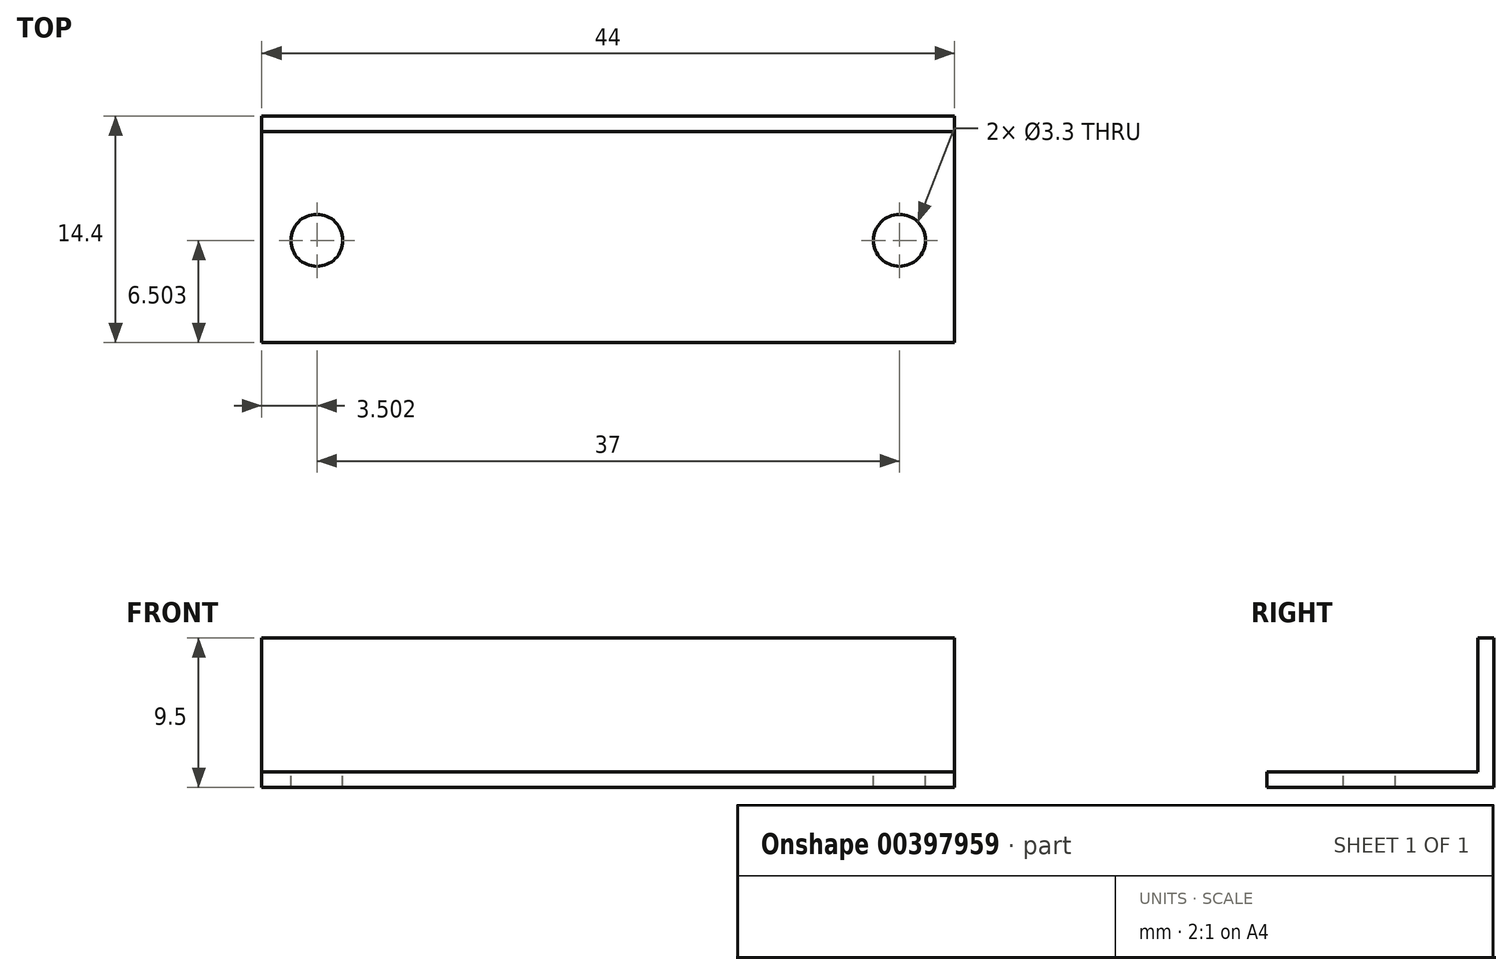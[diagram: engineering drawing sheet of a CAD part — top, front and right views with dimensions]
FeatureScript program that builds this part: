
annotation { "Feature Type Name" : "Feature", "Feature Type Description" : "" }
export const myFeature = defineFeature(function(context is Context, id is Id, definition is map)
    precondition{}
    {
        {
            var Q0;
            Q0=qCreatedBy(makeId("Top.planeOp"),FACE);
            var sketch = newSketch(context, id + "F0", { "sketchPlane" : qUnion([Q0])});
            skLineSegment(sketch, "E0.bottom", {"start": v(-20.63, -28.88) * mm, "end": v(23.37, -28.88) * mm});
            skLineSegment(sketch, "E0.top", {"start": v(-20.63, -43.28) * mm, "end": v(23.37, -43.28) * mm});
            skLineSegment(sketch, "E0.left", {"start": v(-20.63, -28.88) * mm, "end": v(-20.63, -43.28) * mm});
            skLineSegment(sketch, "E0.right", {"start": v(23.37, -28.88) * mm, "end": v(23.37, -43.28) * mm});
            skSolve(sketch);
        }
        {
            var Q0;
            Q0 = qSketchRegion(id + "F0", true);
            extrude(context, id + "F1", {"entities" : qUnion([Q0]), "depth" : 9.5 * mm});
        }
        {
            var Q0;
            Q0=makeQuery(id+"F1.opExtrude","SWEPT_FACE",FACE,{"disambiguationData":[OSD([sQuery(id+"F0.wireOp",EDGE,"E0.right")])]});
            var sketch = newSketch(context, id + "F2", { "sketchPlane" : qUnion([Q0])});
            skPoint(sketch, "E1.oppositeSnap0", {"position": v(-36.08, 0) * mm});
            skLineSegment(sketch, "E2.bottom", {"start": v(-43.28, 9.5) * mm, "end": v(-29.88, 9.5) * mm});
            skLineSegment(sketch, "E2.top", {"start": v(-43.28, 1) * mm, "end": v(-29.88, 1) * mm});
            skLineSegment(sketch, "E2.left", {"start": v(-43.28, 9.5) * mm, "end": v(-43.28, 1) * mm});
            skLineSegment(sketch, "E2.right", {"start": v(-29.88, 9.5) * mm, "end": v(-29.88, 1) * mm});
            skSolve(sketch);
        }
        {
            var Q0;
            Q0 = qSketchRegion(id + "F2", true);
            extrude(context, id + "F3", {"entities" : qUnion([Q0]), "operationType" : NewBodyOperationType.REMOVE, "oppositeDirection" : true, "depth" : 44 * mm});
        }
        {
            var Q0;
            Q0=makeQuery(id+"F3.boolean.opBoolean","COPY",FACE,{"derivedFrom":makeQuery(id+"F3.opExtrude","SWEPT_FACE",FACE,{"disambiguationData":[OSD([sQuery(id+"F2.wireOp",EDGE,"E2.top")])]})});
            var sketch = newSketch(context, id + "F4", { "sketchPlane" : qUnion([Q0])});
            skPoint(sketch, "E3", {"position": v(19.87, -36.78) * mm});
            skPoint(sketch, "E4", {"position": v(-17.13, -36.78) * mm});
            skSolve(sketch);
        }
        {
            var Q0;
            Q0=sQuery(id+"F4.wireOp",VERTEX,"E4");
            var Q1;
            Q1=sQuery(id+"F4.wireOp",VERTEX,"E3");
            var Q2;
            Q2=makeQuery(id+"F1.opExtrude","SWEPT_BODY",BODY,{"disambiguationData":[OSD([sQuery(id+"F0.wireOp",EDGE,"E0.bottom"),sQuery(id+"F0.wireOp",EDGE,"E0.top"),sQuery(id+"F0.wireOp",EDGE,"E0.left"),sQuery(id+"F0.wireOp",EDGE,"E0.right")])]});
            hole(context, id + "F5", {"style" : HoleStyle.SIMPLE, "endStyle" : HoleEndStyle.THROUGH, "standardTappedOrClearance" : lookupTablePath({ "standard" : "ISO", "fit" : "Normal", "size" : "M3", "type" : "Clearance" }), "standardBlindInLast" : lookupTablePath({ "fit" : "Standard", "standard" : "ISO", "size" : "M3", "type" : "Clearance" }), "holeDiameter" : 3.3 * mm, "isTappedThrough" : true, "tappedDepth" : 12 * mm, "tapClearance" : 3, "locations" : qUnion([Q0, Q1]), "scope" : qUnion([Q2])});
        }
    });
